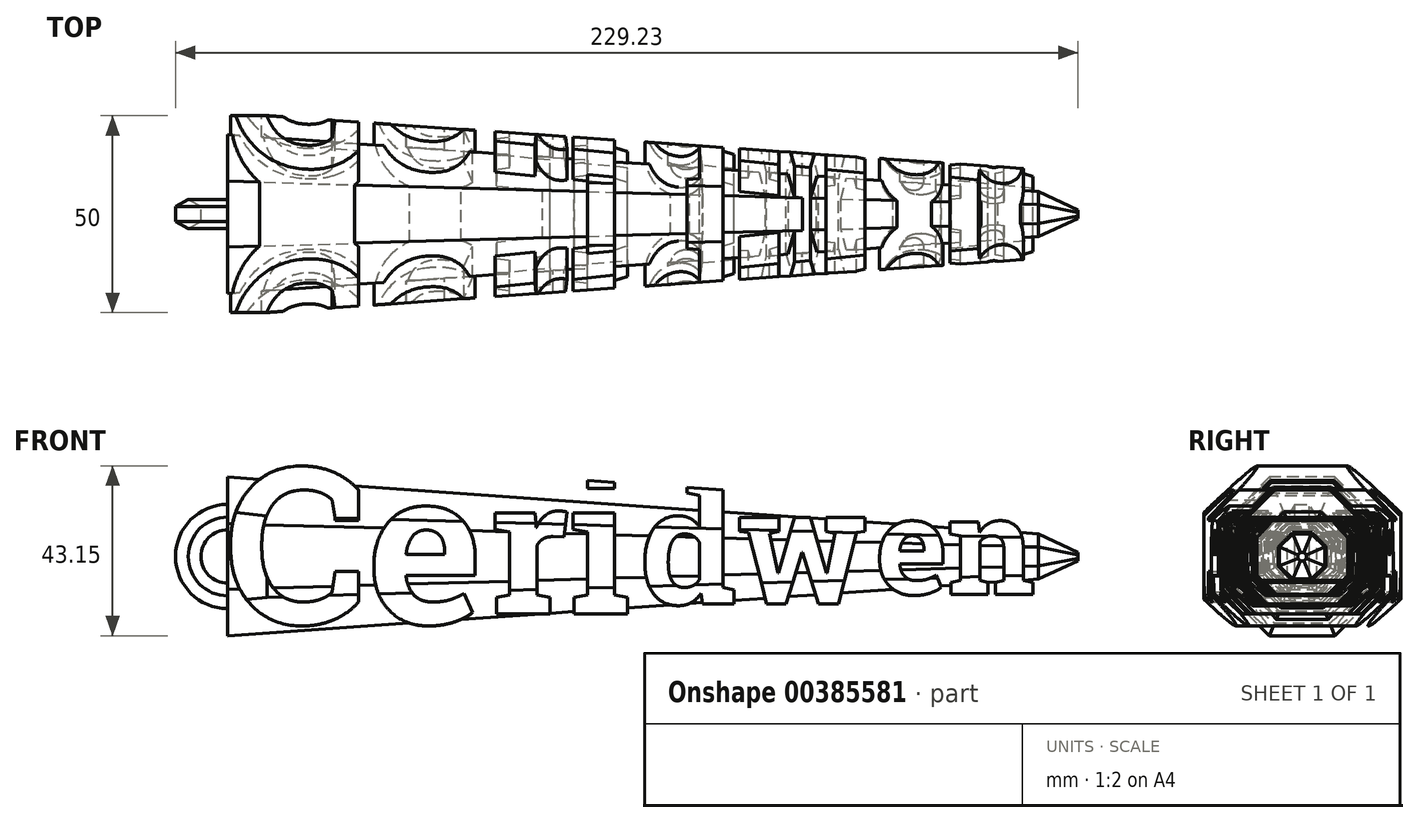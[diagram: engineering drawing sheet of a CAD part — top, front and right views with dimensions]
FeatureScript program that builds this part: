
annotation { "Feature Type Name" : "Feature", "Feature Type Description" : "" }
export const myFeature = defineFeature(function(context is Context, id is Id, definition is map)
    precondition{}
    {
        {
            assignVariable(context, id + "F0", {"name" : "hookPlane", "anyValue" : 103});
        }
        {
            assignVariable(context, id + "F1", {"name" : "halfLength", "anyValue" : 103});
        }
        {
            var Q0;
            Q0=qCreatedBy(makeId("Front.planeOp"),FACE);
            var sketch = newSketch(context, id + "F2", { "sketchPlane" : qUnion([Q0])});
            skText(sketch, "E0", { "text": "Ce", "fontName": "RobotoSlab-Bold.ttf"});
            skPoint(sketch, "E1", {"position": v(-36.7, 0) * mm});
            skText(sketch, "E2", { "text": "ri", "fontName": "RobotoSlab-Bold.ttf"});
            skText(sketch, "E3", { "text": "dw", "fontName": "RobotoSlab-Bold.ttf"});
            skText(sketch, "E4", { "text": "en", "fontName": "RobotoSlab-Bold.ttf"});
            skPoint(sketch, "E5", {"position": v(1.63, 0) * mm});
            skPoint(sketch, "E6", {"position": v(61.5, 0) * mm});
            skLineSegment(sketch, "E7", {"start": v(-103.65, -20) * mm, "end": v(-103.65, -51.65) * mm, "construction": true});
            skLineSegment(sketch, "E8", {"start": v(-103.65, -51.65) * mm, "end": v(103.65, -51.65) * mm, "construction": true});
            skLineSegment(sketch, "E9", {"start": v(103.65, -51.65) * mm, "end": v(103.65, -12.5) * mm, "construction": true});
            skPoint(sketch, "E10", {"position": v(0, -51.65) * mm});
            const initialGuessF2  = {"E0": [-0.10365, -0.02, 1, 0, 0.04], "E2": [-0.0367, -0.0175, 1, 0, 0.035], "E3": [0.00163, -0.015, 1, 0, 0.03], "E4": [0.0615, -0.0125, 1, 0, 0.025]};
            skSetInitialGuess(sketch, initialGuessF2);
            skSolve(sketch);
        }
        {
            var Q0;
            Q0=qSketchRegion(id+"F2",true);
            extrude(context, id + "F3", {"entities" : qUnion([Q0]), "depth" : 25 * mm, "hasSecondDirection" : true, "secondDirectionOppositeDirection" : true, "secondDirectionDepth" : 25 * mm});
        }
        {
            var Q0;
            Q0=qCreatedBy(makeId("Right.planeOp"),FACE);
            var sketch = newSketch(context, id + "F4", { "sketchPlane" : qUnion([Q0])});
            skCircle(sketch, "E11", {"center": v(0, -2.93) * mm, "radius": 12.5 * mm, "construction": true});
            skCircle(sketch, "E12.cCircle", {"center": v(0, -2.93) * mm, "radius": 12.95 * mm, "construction": true});
            skLineSegment(sketch, "E12.0", {"start": v(-5.36, 10.02) * mm, "end": v(5.36, 10.02) * mm});
            skLineSegment(sketch, "E12.1", {"start": v(5.36, 10.02) * mm, "end": v(12.95, 2.43) * mm});
            skLineSegment(sketch, "E12.2", {"start": v(12.95, 2.43) * mm, "end": v(12.95, -8.3) * mm});
            skLineSegment(sketch, "E12.3", {"start": v(12.95, -8.3) * mm, "end": v(5.36, -15.88) * mm});
            skLineSegment(sketch, "E12.4", {"start": v(5.36, -15.88) * mm, "end": v(-5.36, -15.88) * mm});
            skLineSegment(sketch, "E12.5", {"start": v(-5.36, -15.88) * mm, "end": v(-12.95, -8.3) * mm});
            skLineSegment(sketch, "E12.6", {"start": v(-12.95, -8.3) * mm, "end": v(-12.95, 2.43) * mm});
            skLineSegment(sketch, "E12.7", {"start": v(-12.95, 2.43) * mm, "end": v(-5.36, 10.02) * mm});
            skPoint(sketch, "E12.0.midPoint", {"position": v(0, 10.02) * mm});
            skLineSegment(sketch, "E13", {"start": v(0, 20.07) * mm, "end": v(0, 10.02) * mm, "construction": true});
            skSolve(sketch);
        }
        {
            var Q0;
            Q0=qSketchRegion(id+"F4",true);
            var Q1;
            Q1=makeQuery(id+"F3.opExtrude","SWEPT_FACE",FACE,{"disambiguationData":[OSD([sQuery(id+"F2.wireOp",EDGE,"E4.sketch_text.stroke-1")])]});
            extrude(context, id + "F5", {"entities" : qUnion([Q0]), "operationType" : NewBodyOperationType.ADD, "oppositeDirection" : true, "depth" : (getVariable(context, 'halfLength')) * mm, "hasDraft" : true, "draftAngle" : 4 * degree, "hasSecondDirection" : true, "secondDirectionOppositeDirection" : false, "secondDirectionBoundEntityFace" : qUnion([Q1]), "secondDirectionDepth" : (getVariable(context, 'halfLength')) * mm, "hasSecondDirectionDraft" : true, "secondDirectionDraftAngle" : 4 * degree, "secondDirectionDraftPullDirection" : true});
        }
        {
            var Q0;
            Q0=qCreatedBy(makeId("Right.planeOp"),FACE);
            var sketch = newSketch(context, id + "F6", { "sketchPlane" : qUnion([Q0])});
            skCircle(sketch, "E14.cCircle", {"center": v(0, -2.93) * mm, "radius": 18.5 * mm, "construction": true});
            skLineSegment(sketch, "E14.0", {"start": v(-7.66, 15.57) * mm, "end": v(7.66, 15.57) * mm});
            skLineSegment(sketch, "E14.1", {"start": v(7.66, 15.57) * mm, "end": v(18.5, 4.73) * mm});
            skLineSegment(sketch, "E14.2", {"start": v(18.5, 4.73) * mm, "end": v(18.5, -10.6) * mm});
            skLineSegment(sketch, "E14.3", {"start": v(18.5, -10.6) * mm, "end": v(7.66, -21.43) * mm});
            skLineSegment(sketch, "E14.4", {"start": v(7.66, -21.43) * mm, "end": v(-7.66, -21.43) * mm});
            skLineSegment(sketch, "E14.5", {"start": v(-7.66, -21.43) * mm, "end": v(-18.5, -10.6) * mm});
            skLineSegment(sketch, "E14.6", {"start": v(-18.5, -10.6) * mm, "end": v(-18.5, 4.73) * mm});
            skLineSegment(sketch, "E14.7", {"start": v(-18.5, 4.73) * mm, "end": v(-7.66, 15.57) * mm});
            skLineSegment(sketch, "E15.bottom", {"start": v(37.5, 34.57) * mm, "end": v(-37.5, 34.57) * mm});
            skLineSegment(sketch, "E15.top", {"start": v(37.5, -40.43) * mm, "end": v(-37.5, -40.43) * mm});
            skLineSegment(sketch, "E15.left", {"start": v(37.5, 34.57) * mm, "end": v(37.5, -40.43) * mm});
            skLineSegment(sketch, "E15.right", {"start": v(-37.5, 34.57) * mm, "end": v(-37.5, -40.43) * mm});
            skLineSegment(sketch, "E16", {"start": v(0, 20.07) * mm, "end": v(0, -8.52) * mm, "construction": true});
            skSolve(sketch);
        }
        {
            var Q0;
            Q0=makeQuery(id+"F6.imprint","IMPRINT",FACE,{"disambiguationData":[TD([[makeQuery(id+"F6.imprint","IMPRINT",EDGE,{"derivedFrom":sQuery(id+"F6.wireOp",EDGE,"E14.0")}),1.0]])]});
            extrude(context, id + "F7", {"entities" : qUnion([Q0]), "operationType" : NewBodyOperationType.REMOVE, "endBound" : BoundingType.THROUGH_ALL, "depth" : 25 * mm, "hasDraft" : true, "draftAngle" : 4 * degree, "hasSecondDirection" : true, "secondDirectionBound" : SecondDirectionBoundingType.THROUGH_ALL, "secondDirectionOppositeDirection" : true, "secondDirectionDepth" : 25 * mm, "hasSecondDirectionDraft" : true, "secondDirectionDraftAngle" : 4 * degree, "secondDirectionDraftPullDirection" : true});
        }
        {
            var Q0;
            {var subQ0=sQuery(id+"F4.wireOp",EDGE,"E12.3");var subQ1=sQuery(id+"F4.wireOp",EDGE,"E12.2");var subQ2=sQuery(id+"F4.wireOp",EDGE,"E12.4");var subQ3=sQuery(id+"F4.wireOp",EDGE,"E12.5");var subQ4=sQuery(id+"F4.wireOp",EDGE,"E12.6");Q0=makeQuery(id+"F5.boolean.opBoolean","SPLIT",FACE,{"disambiguationData":[TD([makeQuery(id+"F3.opExtrude","SWEPT_FACE",FACE,{"disambiguationData":[OSD([sQuery(id+"F2.wireOp",EDGE,"E4.sketch_text.stroke-0")])]})])],"derivedFrom":makeQuery(id+"F5.opExtrude","CAP_FACE",FACE,{"disambiguationData":[OSD([sQuery(id+"F4.wireOp",EDGE,"E12.0"),sQuery(id+"F4.wireOp",EDGE,"E12.1"),subQ1,subQ0,subQ2,subQ3,subQ4,sQuery(id+"F4.wireOp",EDGE,"E12.7")])],"isStart":true})});}
            var sketch = newSketch(context, id + "F8", { "sketchPlane" : qUnion([Q0])});
            skCircle(sketch, "E17.cCircle", {"center": v(0, -2.93) * mm, "radius": 5.75 * mm, "construction": true});
            skLineSegment(sketch, "E17.0", {"start": v(-2.38, 2.81) * mm, "end": v(2.38, 2.81) * mm});
            skLineSegment(sketch, "E17.1", {"start": v(2.38, 2.81) * mm, "end": v(5.75, -0.55) * mm});
            skLineSegment(sketch, "E17.2", {"start": v(5.75, -0.55) * mm, "end": v(5.75, -5.31) * mm});
            skLineSegment(sketch, "E17.3", {"start": v(5.75, -5.31) * mm, "end": v(2.38, -8.68) * mm});
            skLineSegment(sketch, "E17.4", {"start": v(2.38, -8.68) * mm, "end": v(-2.38, -8.68) * mm});
            skLineSegment(sketch, "E17.5", {"start": v(-2.38, -8.68) * mm, "end": v(-5.75, -5.31) * mm});
            skLineSegment(sketch, "E17.6", {"start": v(-5.75, -5.31) * mm, "end": v(-5.75, -0.55) * mm});
            skLineSegment(sketch, "E17.7", {"start": v(-5.75, -0.55) * mm, "end": v(-2.38, 2.81) * mm});
            skPoint(sketch, "E17.0.midPoint", {"position": v(0, 2.81) * mm});
            skLineSegment(sketch, "E18", {"start": v(0, 19.81) * mm, "end": v(0, -20.35) * mm, "construction": true});
            skSolve(sketch);
        }
        {
            var Q0;
            Q0=qSketchRegion(id+"F8",true);
            extrude(context, id + "F9", {"entities" : qUnion([Q0]), "operationType" : NewBodyOperationType.ADD, "depth" : 10 * mm, "hasDraft" : true, "draftAngle" : 25 * degree, "draftPullDirection" : true});
        }
        {
            var Q0;
            Q0=qCreatedBy(makeId("Right.planeOp"),FACE);
            cPlane(context, id + "F10", {"entities" : qUnion([Q0]), "cplaneType" : CPlaneType.OFFSET, "offset" : (getVariable(context, 'hookPlane')) * mm, "oppositeDirection" : true, "width" : 150 * mm, "height" : 150 * mm});
        }
        {
            var Q0;
            Q0=qCreatedBy(makeId("Front.planeOp"),FACE);
            var sketch = newSketch(context, id + "F11", { "sketchPlane" : qUnion([Q0])});
            skArc(sketch, "E19", {"start": v(-96.39, 4.57) * mm, "mid": v(-113, -2.93) * mm, "end": v(-96.39, -10.43) * mm});
            skLineSegment(sketch, "E20", {"start": v(-96.39, 4.57) * mm, "end": v(-96.39, -10.43) * mm, "construction": true});
            skPoint(sketch, "E21", {"position": v(-96.39, -2.93) * mm});
            skLineSegment(sketch, "E22", {"start": v(-103, 17.22) * mm, "end": v(-103, -23.08) * mm, "construction": true});
            skSolve(sketch);
        }
        {
            var Q0;
            Q0=qCreatedBy(id+"F10.planeOp",FACE);
            var sketch = newSketch(context, id + "F12", { "sketchPlane" : qUnion([Q0])});
            skCircle(sketch, "E23.cCircle", {"center": v(0, 7.07) * mm, "radius": 3.23 * mm, "construction": true});
            skLineSegment(sketch, "E23.0", {"start": v(1.87, 3.84) * mm, "end": v(-1.87, 3.84) * mm});
            skLineSegment(sketch, "E23.1", {"start": v(-1.87, 3.84) * mm, "end": v(-3.73, 7.07) * mm});
            skLineSegment(sketch, "E23.2", {"start": v(-3.73, 7.07) * mm, "end": v(-1.87, 10.3) * mm});
            skLineSegment(sketch, "E23.3", {"start": v(-1.87, 10.3) * mm, "end": v(1.87, 10.3) * mm});
            skLineSegment(sketch, "E23.4", {"start": v(1.87, 10.3) * mm, "end": v(3.73, 7.07) * mm});
            skLineSegment(sketch, "E23.5", {"start": v(3.73, 7.07) * mm, "end": v(1.87, 3.84) * mm});
            skPoint(sketch, "E23.0.midPoint", {"position": v(0, 3.84) * mm});
            skSolve(sketch);
        }
        {
            var Q0;
            Q0=qSketchRegion(id+"F12",true);
            var Q1;
            Q1=qConstructionFilter(qBodyType(qCreatedBy(id+"F11",EDGE),BodyType.WIRE),ConstructionObject.NO);
            sweep(context, id + "F13", {"operationType" : NewBodyOperationType.ADD, "profiles" : qUnion([Q0]), "path" : qUnion([Q1])});
        }
    });
